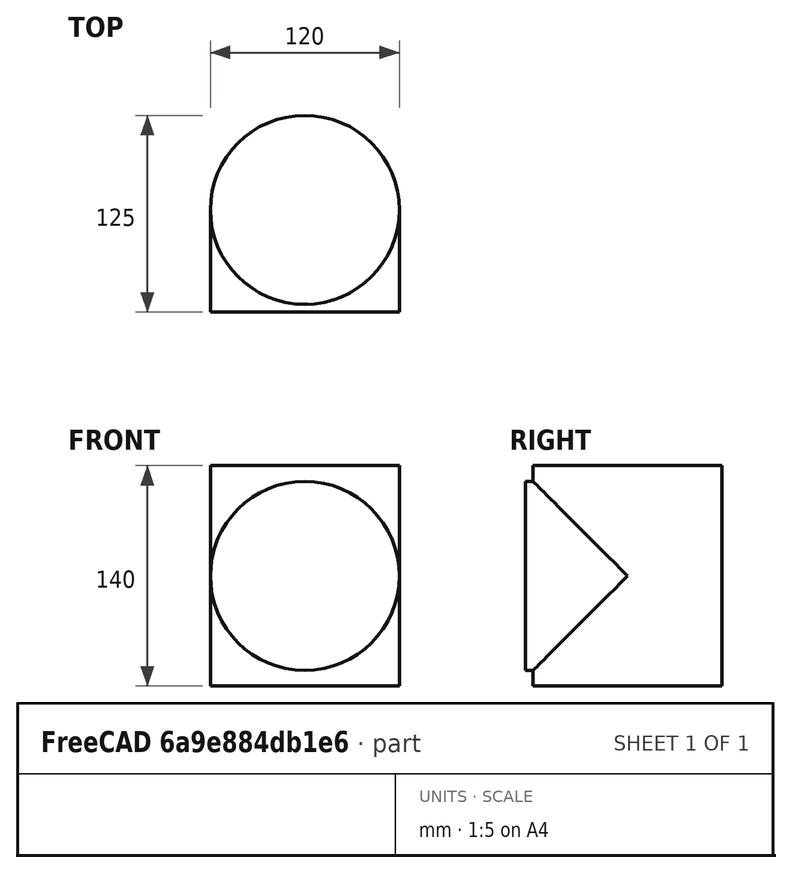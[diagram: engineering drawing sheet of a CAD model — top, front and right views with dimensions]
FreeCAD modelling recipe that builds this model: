
FCSTD DOCUMENT  (FreeCAD 0.19R24366 (Git))
Label: link_1
License: All rights reserved
LicenseURL: http://en.wikipedia.org/wiki/All_rights_reserved
objects: Sketcher::SketchObject×2, PartDesign::Pad×2, PartDesign::Body×1, Mesh::Feature×1
note: 7 computed .brp shape members not serialized (recipe doc carries the construction recipe); baked Part::Feature solids carry a one-line shape summary decoded from their .brp

FEATURE [Sketcher::SketchObject] Sketch
  FullyConstrained = true
  MapMode = 5
  Support = -> [XY_Plane]
  sketch-geometry (1):
    g0: Circle CenterX=0 CenterY=0 CenterZ=0 NormalX=0 NormalY=0 NormalZ=1 AngleXU=0 Radius=60
  constraints (2):
    c: Coincident(g0,g-1)
    c: Diameter(g0) = 120
FEATURE [PartDesign::Pad] Pad
  AllowMultiFace = false
  Direction = (1,1,1)
  Length = 140
  Length2 = 100
  Midplane = true
  Profile = -> Sketch
  Type = 0
FEATURE [Sketcher::SketchObject] Sketch001
  FullyConstrained = true
  MapMode = 5
  Placement = pos=(0,0,0) rot=(1,0,0;1.5708rad)
  Support = -> [XZ_Plane]
  sketch-geometry (1):
    g0: Circle CenterX=0 CenterY=0 CenterZ=0 NormalX=0 NormalY=0 NormalZ=1 AngleXU=0 Radius=60
  constraints (2):
    c: Coincident(g0,g-1)
    c: Diameter(g0) = 120
FEATURE [PartDesign::Pad] Pad001
  AllowMultiFace = false
  BaseFeature = -> Pad
  Direction = (1,1,1)
  Length = 65
  Length2 = 100
  Profile = -> Sketch001
  Type = 0
FEATURE [PartDesign::Body] Body
  Group = -> [Sketch,Pad,Sketch001,Pad001]
  Origin = -> Origin
  Placement = pos=(0,0,70) rot=(0,0,1;0rad)
  Tip = -> Pad001
FEATURE [Mesh::Feature] Mesh  label="Body (Meshed)"
